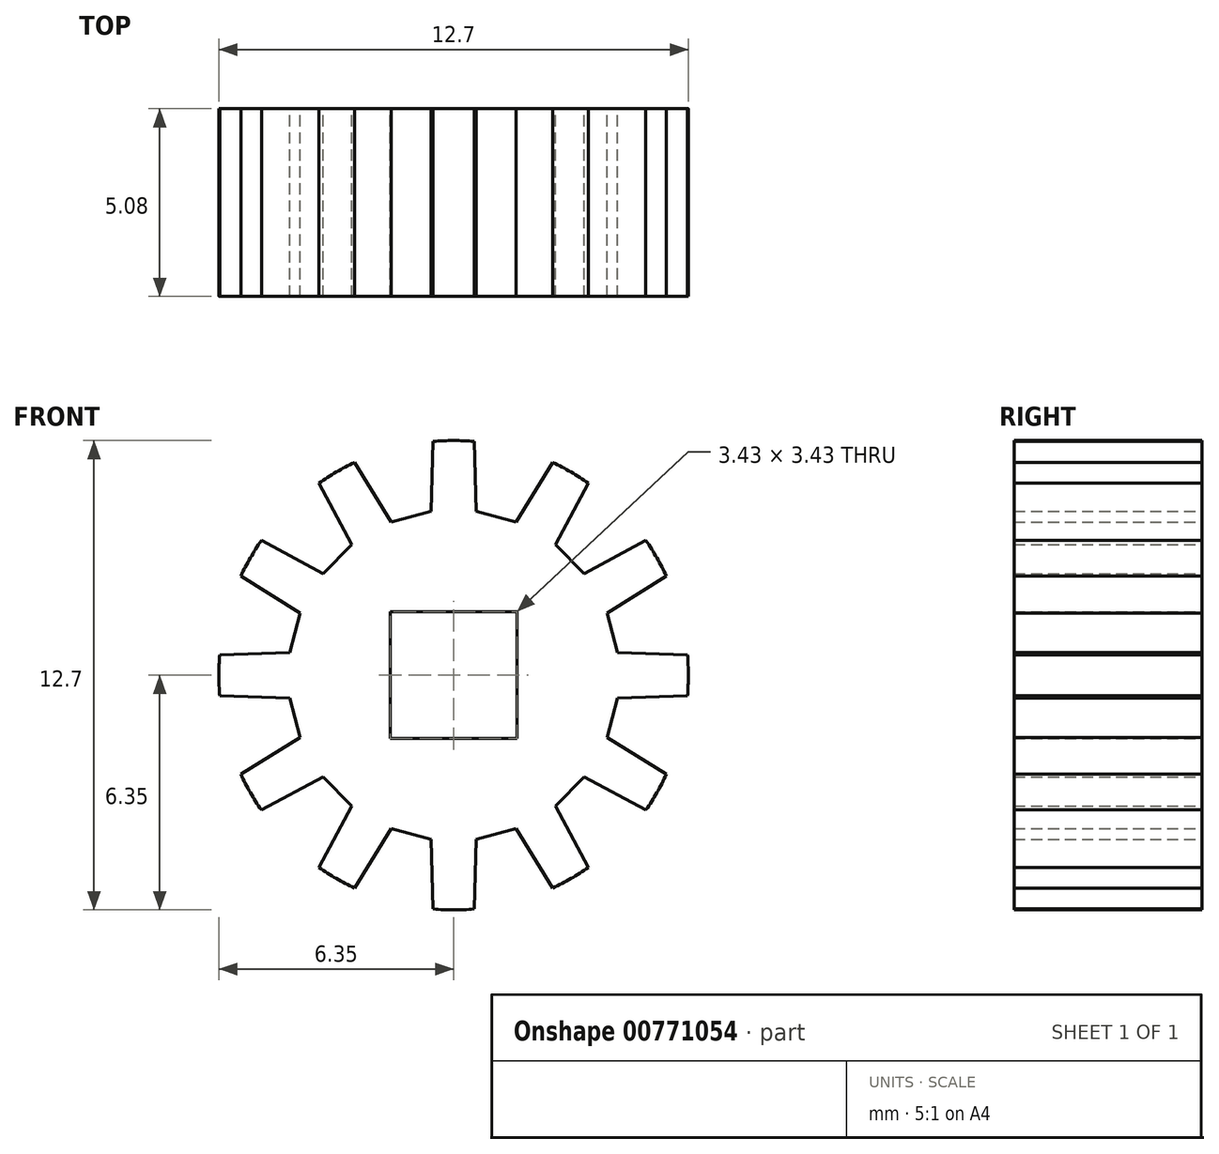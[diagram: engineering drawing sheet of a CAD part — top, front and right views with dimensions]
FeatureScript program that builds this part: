
annotation { "Feature Type Name" : "Feature", "Feature Type Description" : "" }
export const myFeature = defineFeature(function(context is Context, id is Id, definition is map)
    precondition{}
    {
        {
            var Q0;
            Q0=qCreatedBy(makeId("Front.planeOp"),FACE);
            var sketch = newSketch(context, id + "F0", { "sketchPlane" : qUnion([Q0])});
            skCircle(sketch, "E0", {"center": v(0, 0) * mm, "radius": 6.35 * mm});
            skLineSegment(sketch, "E1", {"start": v(0, 0) * mm, "end": v(4.3, 1.15) * mm, "construction": true});
            skLineSegment(sketch, "E2", {"start": v(6.35, 0) * mm, "end": v(6.35, 0.56) * mm});
            skLineSegment(sketch, "E3", {"start": v(6.35, 0) * mm, "end": v(6.35, -0.56) * mm});
            skLineSegment(sketch, "E4", {"start": v(4.3, 1.15) * mm, "end": v(4.44, 0.61) * mm});
            skLineSegment(sketch, "E5", {"start": v(4.3, 1.15) * mm, "end": v(4.15, 1.69) * mm});
            skLineSegment(sketch, "E6", {"start": v(4.44, 0.61) * mm, "end": v(6.35, 0.56) * mm});
            skLineSegment(sketch, "E7", {"start": v(6.35, 0.56) * mm, "end": v(3.9, 0.56) * mm, "construction": true});
            skLineSegment(sketch, "E8", {"start": v(4.44, 0.61) * mm, "end": v(6.76, 0.61) * mm, "construction": true});
            skLineSegment(sketch, "E9", {"start": v(6.35, 0.56) * mm, "end": v(4.15, 1.69) * mm, "construction": true});
            skLineSegment(sketch, "E10", {"start": v(4.44, 0.61) * mm, "end": v(5.78, 2.7) * mm, "construction": true});
            skLineSegment(sketch, "E11", {"start": v(4.15, 1.69) * mm, "end": v(5.78, 2.7) * mm});
            skLineSegment(sketch, "E12", {"start": v(6.35, 0.56) * mm, "end": v(5.78, 2.7) * mm});
            skLineSegment(sketch, "E13.1.0", {"start": v(2.75, 3.54) * mm, "end": v(3.66, 5.22) * mm});
            skLineSegment(sketch, "E13.1.1", {"start": v(5.22, 3.66) * mm, "end": v(3.66, 5.22) * mm});
            skLineSegment(sketch, "E13.1.2", {"start": v(3.14, 3.14) * mm, "end": v(2.75, 3.54) * mm});
            skLineSegment(sketch, "E13.1.3", {"start": v(3.14, 3.14) * mm, "end": v(3.54, 2.75) * mm});
            skLineSegment(sketch, "E13.1.4", {"start": v(3.54, 2.75) * mm, "end": v(5.22, 3.66) * mm});
            skLineSegment(sketch, "E13.1.5", {"start": v(5.5, 3.18) * mm, "end": v(5.78, 2.7) * mm});
            skLineSegment(sketch, "E13.1.6", {"start": v(5.5, 3.18) * mm, "end": v(5.22, 3.66) * mm});
            skLineSegment(sketch, "E13.2.0", {"start": v(0.61, 4.44) * mm, "end": v(0.56, 6.35) * mm});
            skLineSegment(sketch, "E13.2.1", {"start": v(2.7, 5.78) * mm, "end": v(0.56, 6.35) * mm});
            skLineSegment(sketch, "E13.2.2", {"start": v(1.15, 4.3) * mm, "end": v(0.61, 4.44) * mm});
            skLineSegment(sketch, "E13.2.3", {"start": v(1.15, 4.3) * mm, "end": v(1.69, 4.15) * mm});
            skLineSegment(sketch, "E13.2.4", {"start": v(1.69, 4.15) * mm, "end": v(2.7, 5.78) * mm});
            skLineSegment(sketch, "E13.2.5", {"start": v(3.18, 5.5) * mm, "end": v(3.66, 5.22) * mm});
            skLineSegment(sketch, "E13.2.6", {"start": v(3.18, 5.5) * mm, "end": v(2.7, 5.78) * mm});
            skLineSegment(sketch, "E13.3.0", {"start": v(-1.69, 4.15) * mm, "end": v(-2.7, 5.78) * mm});
            skLineSegment(sketch, "E13.3.1", {"start": v(-0.56, 6.35) * mm, "end": v(-2.7, 5.78) * mm});
            skLineSegment(sketch, "E13.3.2", {"start": v(-1.15, 4.3) * mm, "end": v(-1.69, 4.15) * mm});
            skLineSegment(sketch, "E13.3.3", {"start": v(-1.15, 4.3) * mm, "end": v(-0.61, 4.44) * mm});
            skLineSegment(sketch, "E13.3.4", {"start": v(-0.61, 4.44) * mm, "end": v(-0.56, 6.35) * mm});
            skLineSegment(sketch, "E13.3.5", {"start": v(0, 6.35) * mm, "end": v(0.56, 6.35) * mm});
            skLineSegment(sketch, "E13.3.6", {"start": v(0, 6.35) * mm, "end": v(-0.56, 6.35) * mm});
            skLineSegment(sketch, "E13.4.0", {"start": v(-3.54, 2.75) * mm, "end": v(-5.22, 3.66) * mm});
            skLineSegment(sketch, "E13.4.1", {"start": v(-3.66, 5.22) * mm, "end": v(-5.22, 3.66) * mm});
            skLineSegment(sketch, "E13.4.2", {"start": v(-3.14, 3.14) * mm, "end": v(-3.54, 2.75) * mm});
            skLineSegment(sketch, "E13.4.3", {"start": v(-3.14, 3.14) * mm, "end": v(-2.75, 3.54) * mm});
            skLineSegment(sketch, "E13.4.4", {"start": v(-2.75, 3.54) * mm, "end": v(-3.66, 5.22) * mm});
            skLineSegment(sketch, "E13.4.5", {"start": v(-3.17, 5.5) * mm, "end": v(-2.7, 5.78) * mm});
            skLineSegment(sketch, "E13.4.6", {"start": v(-3.17, 5.5) * mm, "end": v(-3.66, 5.22) * mm});
            skLineSegment(sketch, "E13.5.0", {"start": v(-4.44, 0.61) * mm, "end": v(-6.35, 0.56) * mm});
            skLineSegment(sketch, "E13.5.1", {"start": v(-5.78, 2.7) * mm, "end": v(-6.35, 0.56) * mm});
            skLineSegment(sketch, "E13.5.2", {"start": v(-4.3, 1.15) * mm, "end": v(-4.44, 0.61) * mm});
            skLineSegment(sketch, "E13.5.3", {"start": v(-4.3, 1.15) * mm, "end": v(-4.15, 1.69) * mm});
            skLineSegment(sketch, "E13.5.4", {"start": v(-4.15, 1.69) * mm, "end": v(-5.78, 2.7) * mm});
            skLineSegment(sketch, "E13.5.5", {"start": v(-5.5, 3.18) * mm, "end": v(-5.22, 3.66) * mm});
            skLineSegment(sketch, "E13.5.6", {"start": v(-5.5, 3.18) * mm, "end": v(-5.78, 2.7) * mm});
            skLineSegment(sketch, "E13.6.0", {"start": v(-4.15, -1.69) * mm, "end": v(-5.78, -2.7) * mm});
            skLineSegment(sketch, "E13.6.1", {"start": v(-6.35, -0.56) * mm, "end": v(-5.78, -2.7) * mm});
            skLineSegment(sketch, "E13.6.2", {"start": v(-4.3, -1.15) * mm, "end": v(-4.15, -1.69) * mm});
            skLineSegment(sketch, "E13.6.3", {"start": v(-4.3, -1.15) * mm, "end": v(-4.44, -0.61) * mm});
            skLineSegment(sketch, "E13.6.4", {"start": v(-4.44, -0.61) * mm, "end": v(-6.35, -0.56) * mm});
            skLineSegment(sketch, "E13.6.5", {"start": v(-6.35, 0) * mm, "end": v(-6.35, 0.56) * mm});
            skLineSegment(sketch, "E13.6.6", {"start": v(-6.35, 0) * mm, "end": v(-6.35, -0.56) * mm});
            skLineSegment(sketch, "E13.7.0", {"start": v(-2.75, -3.54) * mm, "end": v(-3.66, -5.22) * mm});
            skLineSegment(sketch, "E13.7.1", {"start": v(-5.22, -3.66) * mm, "end": v(-3.66, -5.22) * mm});
            skLineSegment(sketch, "E13.7.2", {"start": v(-3.14, -3.14) * mm, "end": v(-2.75, -3.54) * mm});
            skLineSegment(sketch, "E13.7.3", {"start": v(-3.14, -3.14) * mm, "end": v(-3.54, -2.75) * mm});
            skLineSegment(sketch, "E13.7.4", {"start": v(-3.54, -2.75) * mm, "end": v(-5.22, -3.66) * mm});
            skLineSegment(sketch, "E13.7.5", {"start": v(-5.5, -3.17) * mm, "end": v(-5.78, -2.7) * mm});
            skLineSegment(sketch, "E13.7.6", {"start": v(-5.5, -3.17) * mm, "end": v(-5.22, -3.66) * mm});
            skLineSegment(sketch, "E13.8.0", {"start": v(-0.61, -4.44) * mm, "end": v(-0.56, -6.35) * mm});
            skLineSegment(sketch, "E13.8.1", {"start": v(-2.7, -5.78) * mm, "end": v(-0.56, -6.35) * mm});
            skLineSegment(sketch, "E13.8.2", {"start": v(-1.15, -4.3) * mm, "end": v(-0.61, -4.44) * mm});
            skLineSegment(sketch, "E13.8.3", {"start": v(-1.15, -4.3) * mm, "end": v(-1.69, -4.15) * mm});
            skLineSegment(sketch, "E13.8.4", {"start": v(-1.69, -4.15) * mm, "end": v(-2.7, -5.78) * mm});
            skLineSegment(sketch, "E13.8.5", {"start": v(-3.18, -5.5) * mm, "end": v(-3.66, -5.22) * mm});
            skLineSegment(sketch, "E13.8.6", {"start": v(-3.18, -5.5) * mm, "end": v(-2.7, -5.78) * mm});
            skLineSegment(sketch, "E13.9.0", {"start": v(1.69, -4.15) * mm, "end": v(2.7, -5.78) * mm});
            skLineSegment(sketch, "E13.9.1", {"start": v(0.56, -6.35) * mm, "end": v(2.7, -5.78) * mm});
            skLineSegment(sketch, "E13.9.2", {"start": v(1.15, -4.3) * mm, "end": v(1.69, -4.15) * mm});
            skLineSegment(sketch, "E13.9.3", {"start": v(1.15, -4.3) * mm, "end": v(0.61, -4.44) * mm});
            skLineSegment(sketch, "E13.9.4", {"start": v(0.61, -4.44) * mm, "end": v(0.56, -6.35) * mm});
            skLineSegment(sketch, "E13.9.5", {"start": v(0, -6.35) * mm, "end": v(-0.56, -6.35) * mm});
            skLineSegment(sketch, "E13.9.6", {"start": v(0, -6.35) * mm, "end": v(0.56, -6.35) * mm});
            skLineSegment(sketch, "E13.10.0", {"start": v(3.54, -2.75) * mm, "end": v(5.22, -3.66) * mm});
            skLineSegment(sketch, "E13.10.1", {"start": v(3.66, -5.22) * mm, "end": v(5.22, -3.66) * mm});
            skLineSegment(sketch, "E13.10.2", {"start": v(3.14, -3.14) * mm, "end": v(3.54, -2.75) * mm});
            skLineSegment(sketch, "E13.10.3", {"start": v(3.14, -3.14) * mm, "end": v(2.75, -3.54) * mm});
            skLineSegment(sketch, "E13.10.4", {"start": v(2.75, -3.54) * mm, "end": v(3.66, -5.22) * mm});
            skLineSegment(sketch, "E13.10.5", {"start": v(3.18, -5.5) * mm, "end": v(2.7, -5.78) * mm});
            skLineSegment(sketch, "E13.10.6", {"start": v(3.18, -5.5) * mm, "end": v(3.66, -5.22) * mm});
            skLineSegment(sketch, "E13.11.0", {"start": v(4.44, -0.61) * mm, "end": v(6.35, -0.56) * mm});
            skLineSegment(sketch, "E13.11.1", {"start": v(5.78, -2.7) * mm, "end": v(6.35, -0.56) * mm});
            skLineSegment(sketch, "E13.11.2", {"start": v(4.3, -1.15) * mm, "end": v(4.44, -0.61) * mm});
            skLineSegment(sketch, "E13.11.3", {"start": v(4.3, -1.15) * mm, "end": v(4.15, -1.69) * mm});
            skLineSegment(sketch, "E13.11.4", {"start": v(4.15, -1.69) * mm, "end": v(5.78, -2.7) * mm});
            skLineSegment(sketch, "E13.11.5", {"start": v(5.5, -3.18) * mm, "end": v(5.22, -3.66) * mm});
            skLineSegment(sketch, "E13.11.6", {"start": v(5.5, -3.18) * mm, "end": v(5.78, -2.7) * mm});
            skLineSegment(sketch, "E14.bottom", {"start": v(-1.71, 1.71) * mm, "end": v(1.71, 1.71) * mm});
            skLineSegment(sketch, "E14.top", {"start": v(-1.71, -1.71) * mm, "end": v(1.71, -1.71) * mm});
            skLineSegment(sketch, "E14.left", {"start": v(-1.71, 1.71) * mm, "end": v(-1.71, -1.71) * mm});
            skLineSegment(sketch, "E14.right", {"start": v(1.71, 1.71) * mm, "end": v(1.71, -1.71) * mm});
            skSolve(sketch);
        }
        {
            var Q0;
            {var subQ25=sQuery(id+"F0.wireOp",EDGE,"E4");Q0=makeQuery(id+"F0.imprint","IMPRINT",FACE,{"disambiguationData":[TD([[makeQuery(id+"F0.imprint","IMPRINT",EDGE,{"derivedFrom":subQ25}),-1.0]])]});}
            extrude(context, id + "F1", {"entities" : qUnion([Q0]), "depth" : 5.08 * mm, "offsetDistance" : 25.4 * mm});
        }
    });
